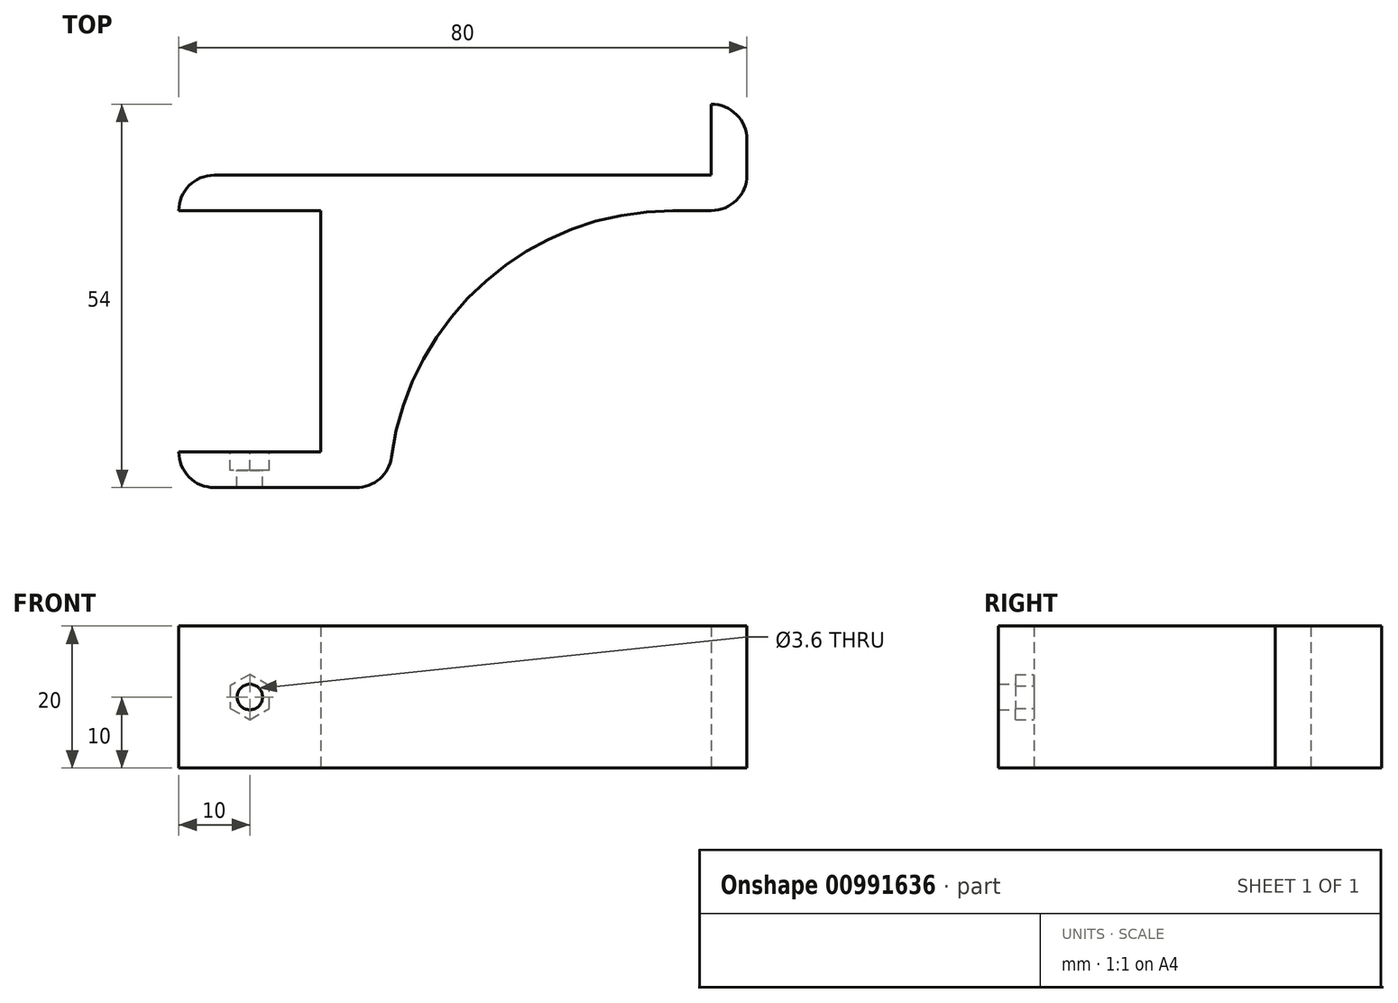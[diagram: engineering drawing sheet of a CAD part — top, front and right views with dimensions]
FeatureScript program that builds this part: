
annotation { "Feature Type Name" : "Feature", "Feature Type Description" : "" }
export const myFeature = defineFeature(function(context is Context, id is Id, definition is map)
    precondition{}
    {
        {
            assignVariable(context, id + "F0", {"name" : "BracketWidth", "anyValue" : 20});
        }
        {
            assignVariable(context, id + "F1", {"name" : "WallThickness", "anyValue" : 5});
        }
        {
            var Q0;
            Q0=qCreatedBy(makeId("Top.planeOp"),FACE);
            var sketch = newSketch(context, id + "F2", { "sketchPlane" : qUnion([Q0])});
            skLineSegment(sketch, "E0", {"start": v(0, 0) * mm, "end": v(20, 0) * mm});
            skLineSegment(sketch, "E1", {"start": v(20, 0) * mm, "end": v(20, -34) * mm});
            skLineSegment(sketch, "E2", {"start": v(20, -34) * mm, "end": v(0, -34) * mm});
            skLineSegment(sketch, "E3", {"start": v(0, -34) * mm, "end": v(0, -39) * mm});
            skLineSegment(sketch, "E4", {"start": v(0, -39) * mm, "end": v(30, -39) * mm});
            skLineSegment(sketch, "E5", {"start": v(30, -39) * mm, "end": v(30, 0) * mm});
            skLineSegment(sketch, "E6", {"start": v(30, 0) * mm, "end": v(80, 0) * mm});
            skLineSegment(sketch, "E7", {"start": v(80, 0) * mm, "end": v(80, 15) * mm});
            skLineSegment(sketch, "E8", {"start": v(80, 15) * mm, "end": v(75, 15) * mm});
            skLineSegment(sketch, "E9", {"start": v(75, 15) * mm, "end": v(75, 5) * mm});
            skLineSegment(sketch, "E10", {"start": v(75, 5) * mm, "end": v(0, 5) * mm});
            skLineSegment(sketch, "E11", {"start": v(0, 5) * mm, "end": v(0, 0) * mm});
            skSolve(sketch);
        }
        {
            var Q0;
            Q0 = qSketchRegion(id + "F2", true);
            extrude(context, id + "F3", {"entities" : qUnion([Q0]), "depth" : (getVariable(context, 'BracketWidth')) * mm, "offsetDistance" : 25 * mm});
        }
        {
            var Q0;
            Q0=makeQuery(id+"F3.opExtrude","SWEPT_EDGE",EDGE,{"disambiguationData":[OSD([sQuery(id+"F2.wireOp",EDGE,"E4"),sQuery(id+"F2.wireOp",EDGE,"E5")])]});
            var Q1;
            Q1=makeQuery(id+"F3.opExtrude","SWEPT_EDGE",EDGE,{"disambiguationData":[OSD([sQuery(id+"F2.wireOp",EDGE,"E6"),sQuery(id+"F2.wireOp",EDGE,"E7")])]});
            var Q2;
            Q2=makeQuery(id+"F3.opExtrude","SWEPT_EDGE",EDGE,{"disambiguationData":[OSD([sQuery(id+"F2.wireOp",EDGE,"E7"),sQuery(id+"F2.wireOp",EDGE,"E8")])]});
            var Q3;
            Q3=makeQuery(id+"F3.opExtrude","SWEPT_EDGE",EDGE,{"disambiguationData":[OSD([sQuery(id+"F2.wireOp",EDGE,"E10"),sQuery(id+"F2.wireOp",EDGE,"E11")])]});
            var Q4;
            Q4=makeQuery(id+"F3.opExtrude","SWEPT_EDGE",EDGE,{"disambiguationData":[OSD([sQuery(id+"F2.wireOp",EDGE,"E3"),sQuery(id+"F2.wireOp",EDGE,"E4")])]});
            fillet(context, id + "F4", {"entities" : qUnion([Q0, Q1, Q2, Q3, Q4]), "radius" : (getVariable(context, 'WallThickness')) * mm, "tangentPropagation" : true, "defaultsChanged" : false, "vertexSettings" : [], "allowEdgeOverflow" : false});
        }
        {
            var Q0;
            Q0=makeQuery(id+"F3.opExtrude","SWEPT_FACE",FACE,{"disambiguationData":[OSD([sQuery(id+"F2.wireOp",EDGE,"E2")])]});
            var sketch = newSketch(context, id + "F5", { "sketchPlane" : qUnion([Q0])});
            skLineSegment(sketch, "E12", {"start": v(0, 20) * mm, "end": v(-20, 0) * mm, "construction": true});
            skLineSegment(sketch, "E13", {"start": v(-20, 0) * mm, "end": v(0, 0) * mm, "construction": true});
            skLineSegment(sketch, "E14", {"start": v(0, 0) * mm, "end": v(-20, 20) * mm, "construction": true});
            skLineSegment(sketch, "E15", {"start": v(-20, 20) * mm, "end": v(0, 20) * mm, "construction": true});
            skPoint(sketch, "E16", {"position": v(-10, 10) * mm});
            skCircle(sketch, "E17.cCircle", {"center": v(-10, 10) * mm, "radius": 2.75 * mm, "construction": true});
            skLineSegment(sketch, "E17.0", {"start": v(-7.25, 11.59) * mm, "end": v(-7.25, 8.41) * mm});
            skLineSegment(sketch, "E17.1", {"start": v(-7.25, 8.41) * mm, "end": v(-10, 6.82) * mm});
            skLineSegment(sketch, "E17.2", {"start": v(-10, 6.82) * mm, "end": v(-12.75, 8.41) * mm});
            skLineSegment(sketch, "E17.3", {"start": v(-12.75, 8.41) * mm, "end": v(-12.75, 11.59) * mm});
            skLineSegment(sketch, "E17.4", {"start": v(-12.75, 11.59) * mm, "end": v(-10, 13.18) * mm});
            skLineSegment(sketch, "E17.5", {"start": v(-10, 13.18) * mm, "end": v(-7.25, 11.59) * mm});
            skPoint(sketch, "E17.0.midPoint", {"position": v(-7.25, 10) * mm});
            skSolve(sketch);
        }
        {
            var Q0;
            Q0 = qSketchRegion(id + "F5", true);
            extrude(context, id + "F6", {"entities" : qUnion([Q0]), "operationType" : NewBodyOperationType.REMOVE, "oppositeDirection" : true, "depth" : 2.6 * mm, "offsetDistance" : 25 * mm});
        }
        {
            var Q0;
            Q0=sQuery(id+"F5.wireOp",VERTEX,"E16");
            var Q1;
            Q1=makeQuery(id+"F3.opExtrude","SWEPT_BODY",BODY,{"disambiguationData":[OSD([sQuery(id+"F2.wireOp",EDGE,"E0"),sQuery(id+"F2.wireOp",EDGE,"E1"),sQuery(id+"F2.wireOp",EDGE,"E2"),sQuery(id+"F2.wireOp",EDGE,"E3"),sQuery(id+"F2.wireOp",EDGE,"E4"),sQuery(id+"F2.wireOp",EDGE,"E5"),sQuery(id+"F2.wireOp",EDGE,"E6"),sQuery(id+"F2.wireOp",EDGE,"E7"),sQuery(id+"F2.wireOp",EDGE,"E8"),sQuery(id+"F2.wireOp",EDGE,"E9"),sQuery(id+"F2.wireOp",EDGE,"E10"),sQuery(id+"F2.wireOp",EDGE,"E11")])]});
            hole(context, id + "F7", {"style" : HoleStyle.SIMPLE, "endStyle" : HoleEndStyle.BLIND, "standardTappedOrClearance" : lookupTablePath({ "fit" : "Loose", "standard" : "ISO", "size" : "M3", "type" : "Clearance" }), "standardBlindInLast" : lookupTablePath({ "fit" : "Loose", "standard" : "ISO", "engagement" : "75%", "pitch" : "0.5 mm", "size" : "M3", "type" : "Clearance & tapped" }), "holeDiameter" : 3.6 * mm, "majorDiameter" : 5 * mm, "holeDepth" : 10 * mm, "isTappedThrough" : true, "tappedDepth" : 12 * mm, "tapClearance" : 3, "startFromSketch" : true, "locations" : qUnion([Q0]), "scope" : qUnion([Q1])});
        }
        {
            var Q0;
            Q0=makeQuery(id+"F3.opExtrude","SWEPT_EDGE",EDGE,{"disambiguationData":[OSD([sQuery(id+"F2.wireOp",EDGE,"E5"),sQuery(id+"F2.wireOp",EDGE,"E6")])]});
            fillet(context, id + "F8", {"entities" : qUnion([Q0]), "tangentPropagation" : true, "radius" : 40 * mm, "defaultsChanged" : true, "vertexSettings" : [], "allowEdgeOverflow" : false});
        }
    });
